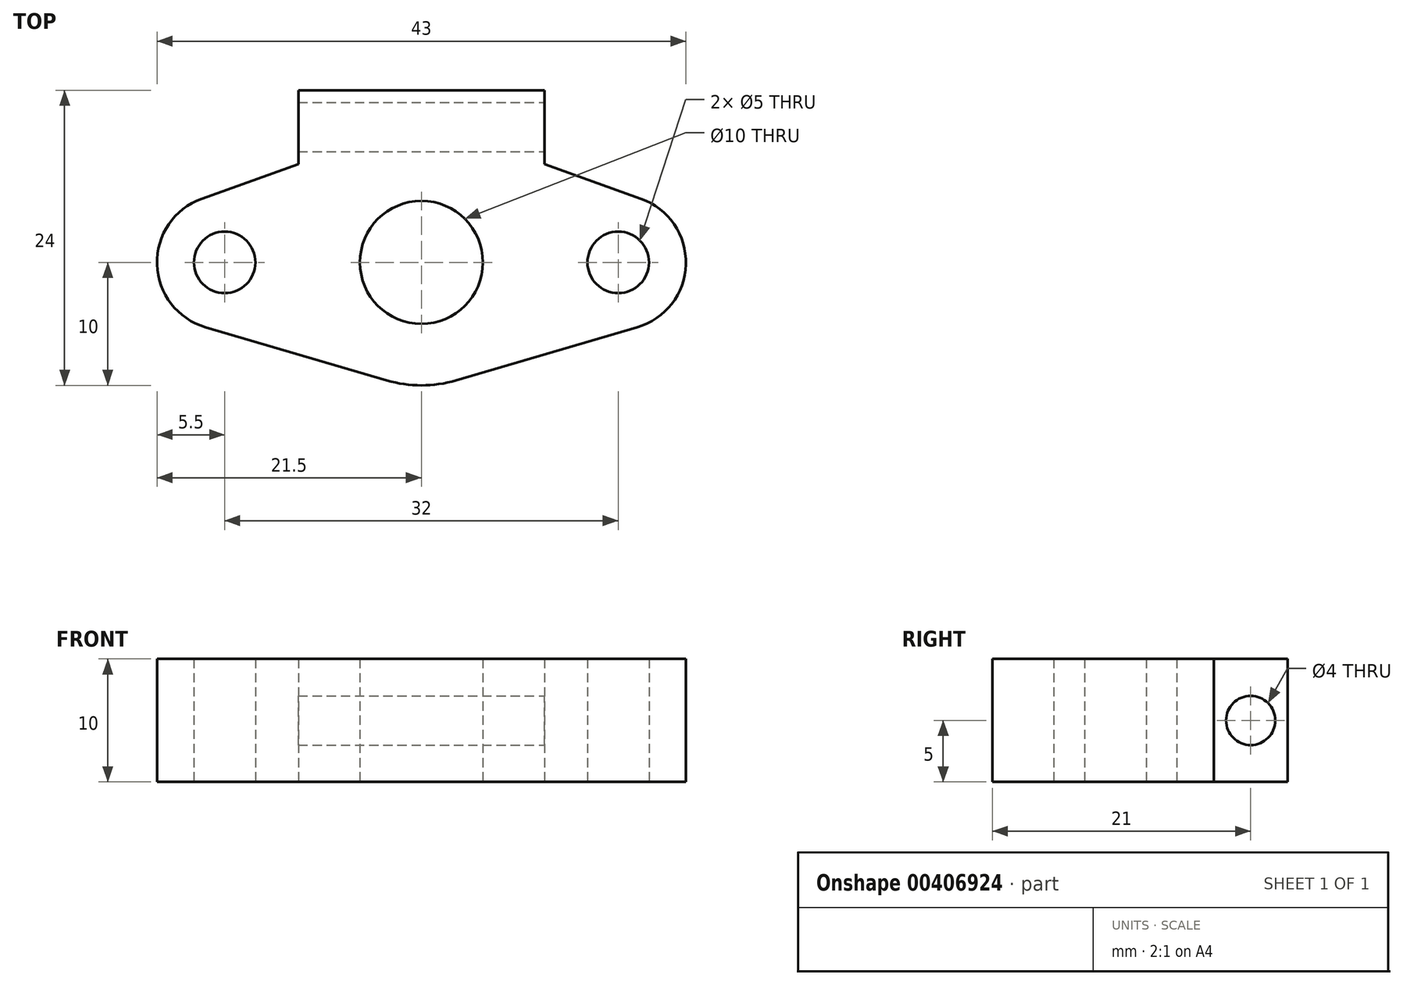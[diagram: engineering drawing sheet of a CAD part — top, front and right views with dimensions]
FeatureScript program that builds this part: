
annotation { "Feature Type Name" : "Feature", "Feature Type Description" : "" }
export const myFeature = defineFeature(function(context is Context, id is Id, definition is map)
    precondition{}
    {
        {
            var Q0;
            Q0=qCreatedBy(makeId("Top.planeOp"),FACE);
            var sketch = newSketch(context, id + "F0", { "sketchPlane" : qUnion([Q0])});
            skCircle(sketch, "E0", {"center": v(0, 0) * mm, "radius": 5 * mm});
            skCircle(sketch, "E1", {"center": v(-16, 0) * mm, "radius": 2.5 * mm});
            skLineSegment(sketch, "E2", {"start": v(-21.5, 17.75) * mm, "end": v(-21.5, -23.86) * mm, "construction": true});
            skLineSegment(sketch, "E3", {"start": v(-17.55, -5.28) * mm, "end": v(-2.81, -9.6) * mm});
            skLineSegment(sketch, "E4", {"start": v(-31.17, 14) * mm, "end": v(35.28, 14) * mm, "construction": true});
            skLineSegment(sketch, "E5", {"start": v(0, 14) * mm, "end": v(-10, 14) * mm});
            skLineSegment(sketch, "E6", {"start": v(-10, 14) * mm, "end": v(-10, 8) * mm});
            skLineSegment(sketch, "E7", {"start": v(-10, 8) * mm, "end": v(-17.86, 5.18) * mm});
            skArc(sketch, "E8", {"start": v(-17.55, -5.28) * mm, "mid": v(-10.5, 0.16) * mm, "end": v(-17.86, 5.18) * mm, "construction": true});
            skArc(sketch, "E9", {"start": v(-17.86, 5.18) * mm, "mid": v(-21.5, -0.16) * mm, "end": v(-17.55, -5.28) * mm});
            skLineSegment(sketch, "E10.MirrorCS", {"start": v(10, 14) * mm, "end": v(10, 8) * mm});
            skLineSegment(sketch, "E11.MirrorCS", {"start": v(10, 8) * mm, "end": v(17.86, 5.18) * mm});
            skArc(sketch, "E12.MirrorCS", {"start": v(17.86, 5.18) * mm, "mid": v(21.5, -0.16) * mm, "end": v(17.55, -5.28) * mm});
            skLineSegment(sketch, "E13.MirrorCS", {"start": v(17.55, -5.28) * mm, "end": v(2.81, -9.6) * mm});
            skCircle(sketch, "E14.MirrorC", {"center": v(16, 0) * mm, "radius": 2.5 * mm});
            skArc(sketch, "E15", {"start": v(-2.81, -9.6) * mm, "mid": v(0, -10) * mm, "end": v(2.81, -9.6) * mm});
            skArc(sketch, "E16", {"start": v(2.81, -9.6) * mm, "mid": v(0, 10) * mm, "end": v(-2.81, -9.6) * mm, "construction": true});
            skLineSegment(sketch, "E17", {"start": v(0, 14) * mm, "end": v(10, 14) * mm});
            skSolve(sketch);
        }
        {
            var Q0;
            Q0 = qSketchRegion(id + "F0", true);
            extrude(context, id + "F1", {"entities" : qUnion([Q0]), "depth" : 10 * mm});
        }
        {
            var Q0;
            Q0=makeQuery(id+"F1.opExtrude","SWEPT_FACE",FACE,{"disambiguationData":[OSD([sQuery(id+"F0.wireOp",EDGE,"E10.MirrorCS")])]});
            var sketch = newSketch(context, id + "F2", { "sketchPlane" : qUnion([Q0])});
            skLineSegment(sketch, "E18", {"start": v(11, 10) * mm, "end": v(11, 0) * mm, "construction": true});
            skCircle(sketch, "E19", {"center": v(11, 5) * mm, "radius": 2 * mm});
            skSolve(sketch);
        }
        {
            var Q0;
            Q0 = qSketchRegion(id + "F2", true);
            extrude(context, id + "F3", {"entities" : qUnion([Q0]), "operationType" : NewBodyOperationType.REMOVE, "oppositeDirection" : true, "depth" : 25 * mm});
        }
    });
